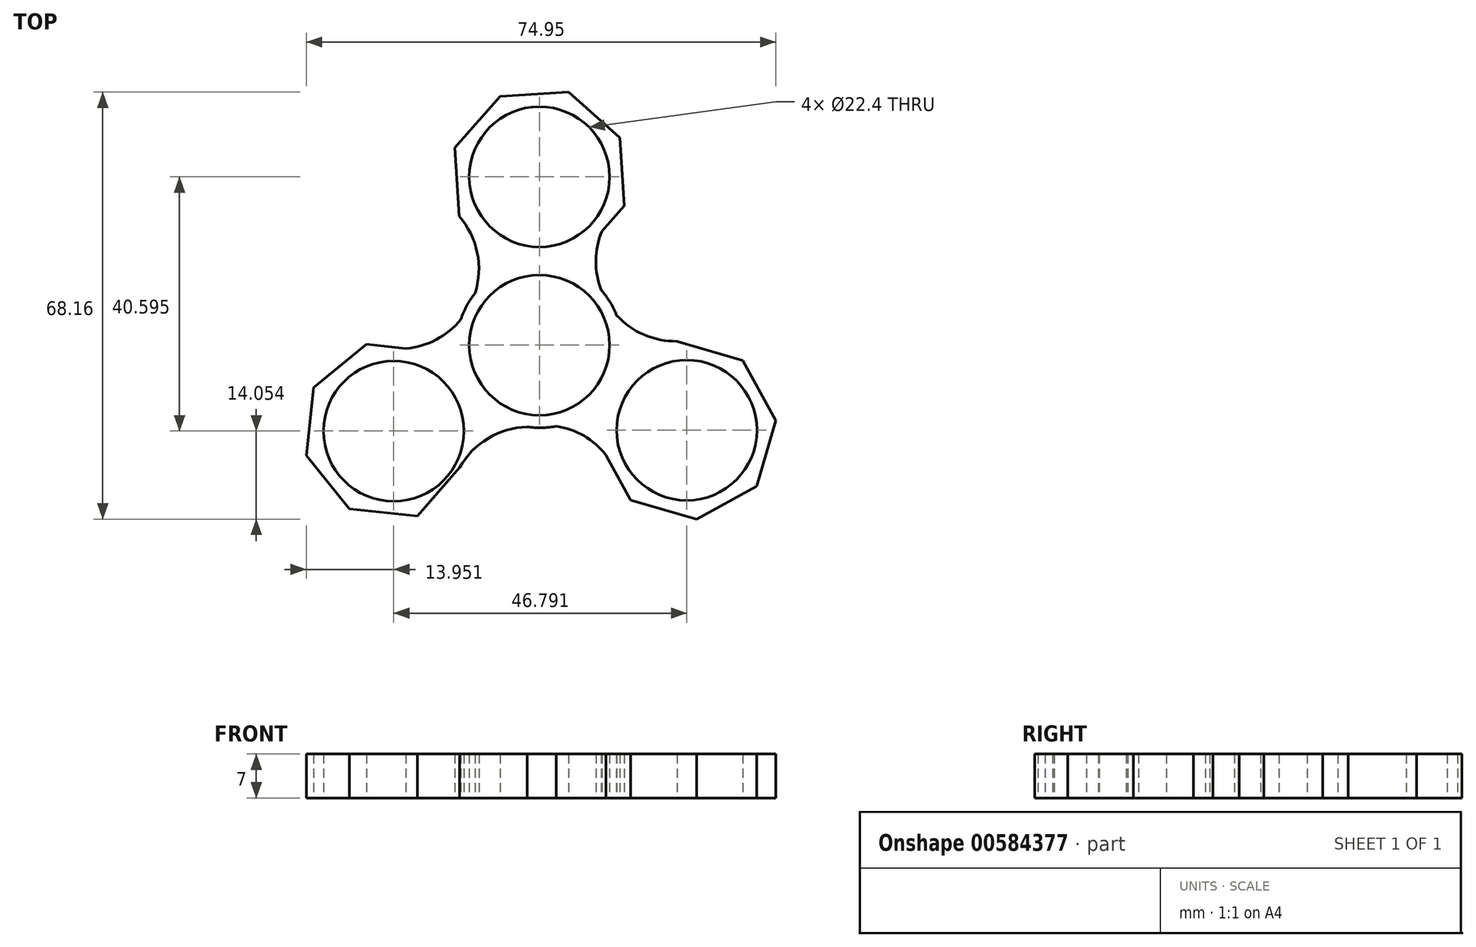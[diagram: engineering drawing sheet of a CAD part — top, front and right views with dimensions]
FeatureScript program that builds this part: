
annotation { "Feature Type Name" : "Feature", "Feature Type Description" : "" }
export const myFeature = defineFeature(function(context is Context, id is Id, definition is map)
    precondition{}
    {
        {
            var Q0;
            Q0=qCreatedBy(makeId("Top.planeOp"),FACE);
            var sketch = newSketch(context, id + "F0", { "sketchPlane" : qUnion([Q0])});
            skCircle(sketch, "E0", {"center": v(0, 0) * mm, "radius": 11.2 * mm});
            skCircle(sketch, "E1", {"center": v(0, 0) * mm, "radius": 13.2 * mm});
            skCircle(sketch, "E2", {"center": v(0, 26.87) * mm, "radius": 11.2 * mm});
            skCircle(sketch, "E3.1.0", {"center": v(-23.27, -13.73) * mm, "radius": 11.2 * mm});
            skCircle(sketch, "E3.2.0", {"center": v(23.52, -13.58) * mm, "radius": 11.2 * mm});
            skArc(sketch, "E3.2.1", {"start": v(11.94, -19.92) * mm, "mid": v(12.27, -20.49) * mm, "end": v(12.63, -21.04) * mm});
            skPoint(sketch, "E3.center", {"position": v(0.08, -0.15) * mm});
            skLineSegment(sketch, "E4.0", {"start": v(13.51, 22.22) * mm, "end": v(9.96, 18.2) * mm});
            skLineSegment(sketch, "E4.3", {"start": v(-12.84, 20.6) * mm, "end": v(-13.51, 31.52) * mm});
            skLineSegment(sketch, "E4.4", {"start": v(-13.51, 31.52) * mm, "end": v(-6.27, 39.7) * mm});
            skLineSegment(sketch, "E4.5", {"start": v(-6.27, 39.7) * mm, "end": v(4.65, 40.38) * mm});
            skLineSegment(sketch, "E4.6", {"start": v(4.65, 40.38) * mm, "end": v(12.84, 33.13) * mm});
            skLineSegment(sketch, "E4.7", {"start": v(12.84, 33.13) * mm, "end": v(13.51, 22.22) * mm});
            skPoint(sketch, "E4.0.midPoint", {"position": v(9.89, 18.12) * mm});
            skArc(sketch, "E5.cCircle", {"start": v(11.94, -19.92) * mm, "mid": v(12.27, -20.49) * mm, "end": v(12.63, -21.04) * mm, "construction": true});
            skLineSegment(sketch, "E5.0", {"start": v(34.66, -22.53) * mm, "end": v(25.06, -27.78) * mm});
            skLineSegment(sketch, "E5.1", {"start": v(25.06, -27.78) * mm, "end": v(14.57, -24.71) * mm});
            skLineSegment(sketch, "E5.2", {"start": v(14.57, -24.71) * mm, "end": v(10.64, -17.54) * mm});
            skLineSegment(sketch, "E5.5", {"start": v(21.98, 0.62) * mm, "end": v(32.48, -2.45) * mm});
            skLineSegment(sketch, "E5.6", {"start": v(32.48, -2.45) * mm, "end": v(37.73, -12.04) * mm});
            skLineSegment(sketch, "E5.7", {"start": v(37.73, -12.04) * mm, "end": v(34.66, -22.53) * mm});
            skPoint(sketch, "E5.0.midPoint", {"position": v(29.86, -25.16) * mm});
            skLineSegment(sketch, "E6.0", {"start": v(-12.73, -19.54) * mm, "end": v(-19.46, -27.28) * mm});
            skLineSegment(sketch, "E6.1", {"start": v(-19.46, -27.28) * mm, "end": v(-30.34, -26.14) * mm});
            skLineSegment(sketch, "E6.2", {"start": v(-30.34, -26.14) * mm, "end": v(-37.22, -17.64) * mm});
            skLineSegment(sketch, "E6.3", {"start": v(-37.22, -17.64) * mm, "end": v(-36.08, -6.77) * mm});
            skLineSegment(sketch, "E6.4", {"start": v(-36.08, -6.77) * mm, "end": v(-27.58, 0.12) * mm});
            skLineSegment(sketch, "E6.5", {"start": v(-27.58, 0.12) * mm, "end": v(-21.3, -0.54) * mm});
            skPoint(sketch, "E6.0.midPoint", {"position": v(-16.1, -23.4) * mm});
            skArc(sketch, "E7.1.0", {"start": v(-27.04, 0.27) * mm, "mid": v(-26.62, 0.11) * mm, "end": v(-26.2, -0.03) * mm});
            skPoint(sketch, "E7.center", {"position": v(-1.2, 0.56) * mm});
            skArc(sketch, "E8.trimOffspring", {"start": v(-21.4, -0.55) * mm, "mid": v(-22.97, -0.4) * mm, "end": v(-24.53, -0.42) * mm, "construction": true});
            skArc(sketch, "E9.trimOffspring", {"start": v(-21.4, -0.55) * mm, "mid": v(-22.97, -0.4) * mm, "end": v(-24.53, -0.42) * mm});
            skArc(sketch, "E10.trimOffspring", {"start": v(-21.4, -0.55) * mm, "mid": v(-16.5, 0.87) * mm, "end": v(-12.55, 4.1) * mm});
            skArc(sketch, "E11.trimOffspring", {"start": v(-1.97, -13.05) * mm, "mid": v(-8.2, -14.88) * mm, "end": v(-12.73, -19.54) * mm});
            skPoint(sketch, "E12.orphan", {"position": v(11.98, -21.67) * mm});
            skArc(sketch, "E13.trimOffspring", {"start": v(12.3, 4.82) * mm, "mid": v(16.68, 1.67) * mm, "end": v(21.98, 0.62) * mm});
            skArc(sketch, "E14.trimOffspring", {"start": v(-10.27, 8.29) * mm, "mid": v(-9.94, 14.78) * mm, "end": v(-12.84, 20.6) * mm});
            skArc(sketch, "E15.trimOffspring", {"start": v(9.96, 18.2) * mm, "mid": v(9, 13.5) * mm, "end": v(9.85, 8.79) * mm});
            skArc(sketch, "E16.trimOffspring", {"start": v(10.64, -17.54) * mm, "mid": v(7.1, -14.49) * mm, "end": v(2.69, -12.92) * mm});
            skPoint(sketch, "E17.orphan", {"position": v(6.27, 14.03) * mm});
            skSolve(sketch);
        }
        {
            var Q0;
            Q0 = qSketchRegion(id + "F0", true);
            extrude(context, id + "F1", {"entities" : qUnion([Q0]), "depth" : 7 * mm, "offsetDistance" : 25 * mm});
        }
    });
